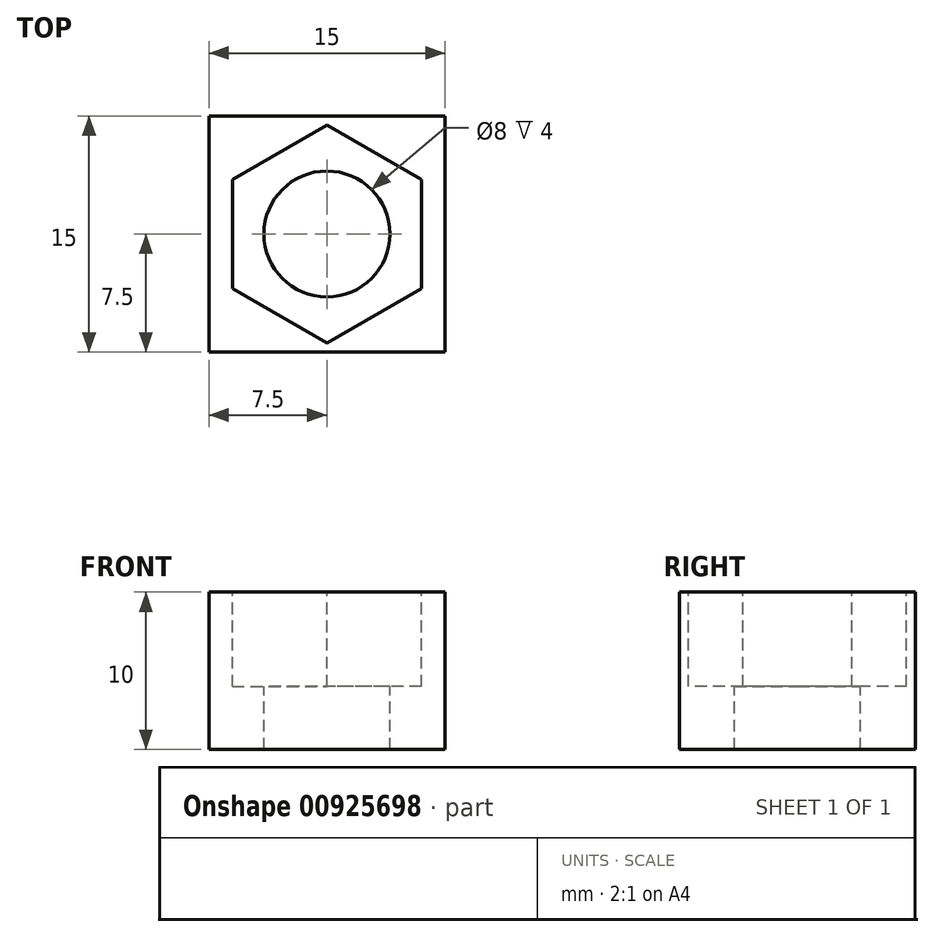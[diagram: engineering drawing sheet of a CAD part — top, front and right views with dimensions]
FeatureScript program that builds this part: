
annotation { "Feature Type Name" : "Feature", "Feature Type Description" : "" }
export const myFeature = defineFeature(function(context is Context, id is Id, definition is map)
    precondition{}
    {
        {
            var Q0;
            Q0=qCreatedBy(makeId("Top.planeOp"),FACE);
            var sketch = newSketch(context, id + "F0", { "sketchPlane" : qUnion([Q0])});
            skLineSegment(sketch, "E0.bottom", {"start": v(7.5, -7.5) * mm, "end": v(-7.5, -7.5) * mm});
            skLineSegment(sketch, "E0.top", {"start": v(7.5, 7.5) * mm, "end": v(-7.5, 7.5) * mm});
            skLineSegment(sketch, "E0.left", {"start": v(7.5, -7.5) * mm, "end": v(7.5, 7.5) * mm});
            skLineSegment(sketch, "E0.right", {"start": v(-7.5, -7.5) * mm, "end": v(-7.5, 7.5) * mm});
            skPoint(sketch, "E0.middle", {"position": v(0, 0) * mm});
            skSolve(sketch);
        }
        {
            var Q0;
            Q0=makeQuery(id+"F0.imprint","IMPRINT",FACE,{"disambiguationData":[TD([[makeQuery(id+"F0.imprint","IMPRINT",EDGE,{"derivedFrom":sQuery(id+"F0.wireOp",EDGE,"E0.bottom")}),-1.0]])]});
            extrude(context, id + "F1", {"entities" : qUnion([Q0]), "depth" : 10 * mm, "offsetDistance" : 25 * mm});
        }
        {
            var Q0;
            Q0=makeQuery(id+"F1.opExtrude","CAP_FACE",FACE,{"disambiguationData":[OSD([sQuery(id+"F0.wireOp",EDGE,"E0.bottom"),sQuery(id+"F0.wireOp",EDGE,"E0.top"),sQuery(id+"F0.wireOp",EDGE,"E0.left"),sQuery(id+"F0.wireOp",EDGE,"E0.right")])],"isStart":false});
            var sketch = newSketch(context, id + "F2", { "sketchPlane" : qUnion([Q0])});
            skCircle(sketch, "E1.cCircle", {"center": v(0, 0) * mm, "radius": 6 * mm, "construction": true});
            skLineSegment(sketch, "E1.0", {"start": v(6, -3.46) * mm, "end": v(0, -6.93) * mm});
            skLineSegment(sketch, "E1.1", {"start": v(0, -6.93) * mm, "end": v(-6, -3.46) * mm});
            skLineSegment(sketch, "E1.2", {"start": v(-6, -3.46) * mm, "end": v(-6, 3.46) * mm});
            skLineSegment(sketch, "E1.3", {"start": v(-6, 3.46) * mm, "end": v(0, 6.93) * mm});
            skLineSegment(sketch, "E1.4", {"start": v(0, 6.93) * mm, "end": v(6, 3.46) * mm});
            skLineSegment(sketch, "E1.5", {"start": v(6, 3.46) * mm, "end": v(6, -3.46) * mm});
            skPoint(sketch, "E1.0.midPoint", {"position": v(3, -5.2) * mm});
            skSolve(sketch);
        }
        {
            var Q0;
            Q0=makeQuery(id+"F2.imprint","IMPRINT",FACE,{"disambiguationData":[TD([[makeQuery(id+"F2.imprint","IMPRINT",EDGE,{"derivedFrom":sQuery(id+"F2.wireOp",EDGE,"E1.0")}),-1.0]])]});
            extrude(context, id + "F3", {"entities" : qUnion([Q0]), "operationType" : NewBodyOperationType.REMOVE, "oppositeDirection" : true, "depth" : 6 * mm, "offsetDistance" : 25 * mm});
        }
        {
            var Q0;
            Q0=makeQuery(id+"F3.boolean.opBoolean","COPY",FACE,{"derivedFrom":makeQuery(id+"F3.opExtrude","CAP_FACE",FACE,{"disambiguationData":[OSD([sQuery(id+"F2.wireOp",EDGE,"E1.0"),sQuery(id+"F2.wireOp",EDGE,"E1.1"),sQuery(id+"F2.wireOp",EDGE,"E1.2"),sQuery(id+"F2.wireOp",EDGE,"E1.3"),sQuery(id+"F2.wireOp",EDGE,"E1.4"),sQuery(id+"F2.wireOp",EDGE,"E1.5")])],"isStart":false})});
            var sketch = newSketch(context, id + "F4", { "sketchPlane" : qUnion([Q0])});
            skCircle(sketch, "E2", {"center": v(0, 0) * mm, "radius": 4 * mm});
            skSolve(sketch);
        }
        {
            var Q0;
            Q0=makeQuery(id+"F4.imprint","IMPRINT",FACE,{"disambiguationData":[TD([[makeQuery(id+"F4.imprint","IMPRINT",EDGE,{"derivedFrom":sQuery(id+"F4.wireOp",EDGE,"E2")}),1.0]])]});
            extrude(context, id + "F5", {"entities" : qUnion([Q0]), "operationType" : NewBodyOperationType.REMOVE, "oppositeDirection" : true, "depth" : 25 * mm, "offsetDistance" : 25 * mm});
        }
    });
